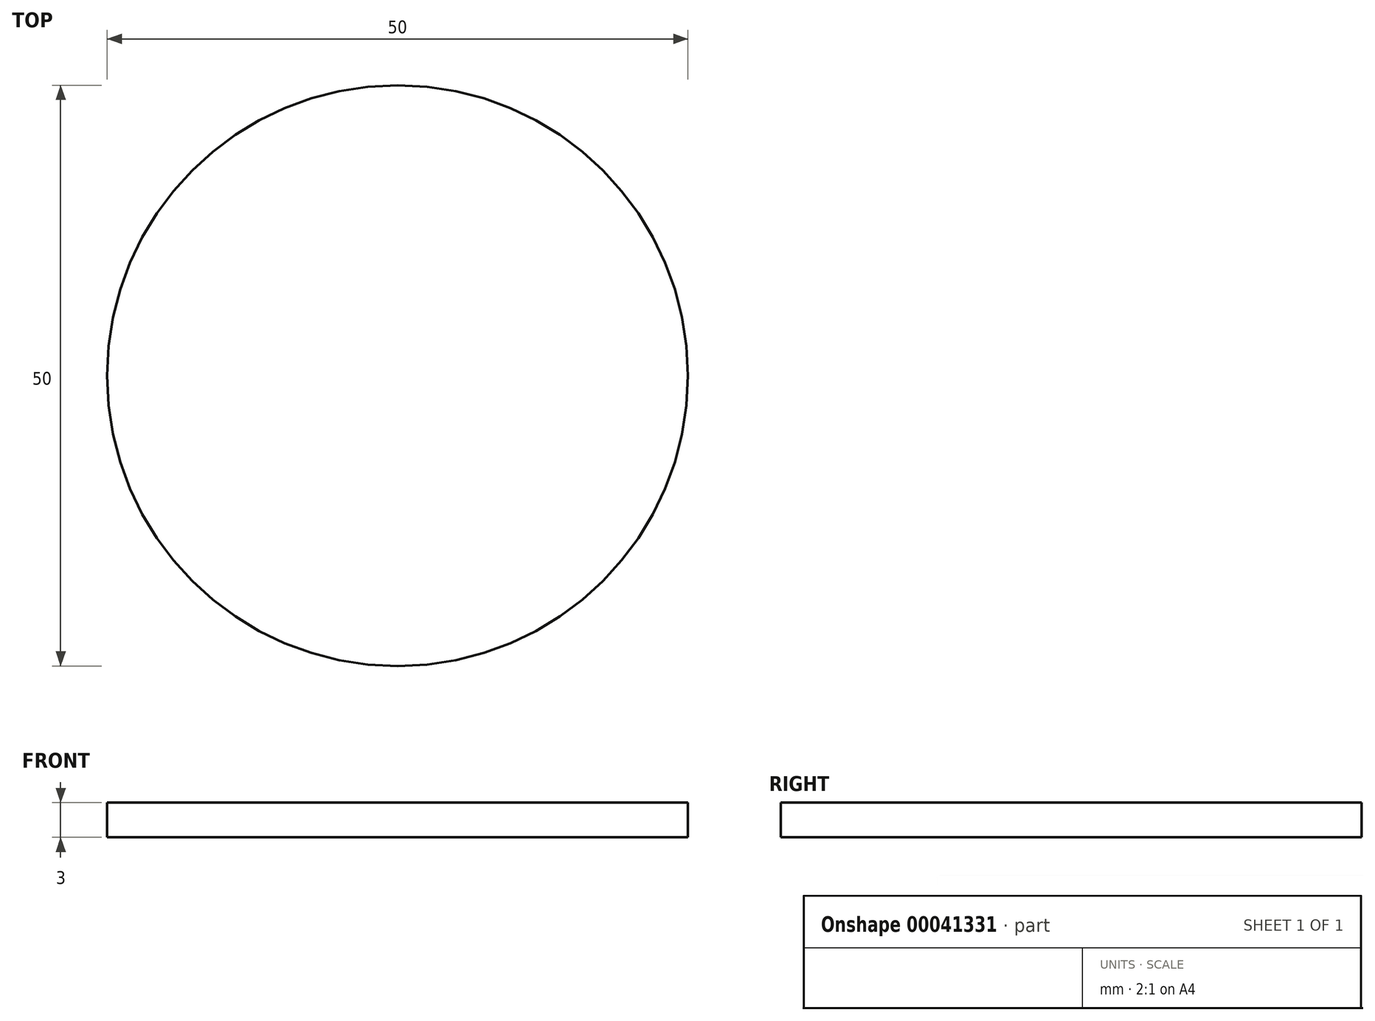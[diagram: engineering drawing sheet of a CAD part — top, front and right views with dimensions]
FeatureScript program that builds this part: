
annotation { "Feature Type Name" : "Feature", "Feature Type Description" : "" }
export const myFeature = defineFeature(function(context is Context, id is Id, definition is map)
    precondition{}
    {
        {
            var Q0;
            Q0=qCreatedBy(makeId("Front.planeOp"),FACE);
            var sketch = newSketch(context, id + "F0", { "sketchPlane" : qUnion([Q0])});
            skLineSegment(sketch, "E0", {"start": v(0, 0) * mm, "end": v(-25, 0) * mm});
            skLineSegment(sketch, "E1", {"start": v(-25, 0) * mm, "end": v(-25, 3) * mm});
            skLineSegment(sketch, "E2", {"start": v(-25, 3) * mm, "end": v(0, 3) * mm});
            skLineSegment(sketch, "E3", {"start": v(0, 3) * mm, "end": v(0, 0) * mm});
            skSolve(sketch);
        }
        {
            var Q0;
            Q0=makeQuery(id+"F0.imprint","IMPRINT",FACE,{"disambiguationData":[TD([[makeQuery(id+"F0.imprint","IMPRINT",EDGE,{"derivedFrom":sQuery(id+"F0.wireOp",EDGE,"E0")}),-1.0]])]});
            var Q1;
            Q1=sQuery(id+"F0.wireOp",EDGE,"E3");
            revolve(context, id + "F1", {"entities" : qUnion([Q0]), "axis" : qUnion([Q1]), "revolveType" : RevolveType.FULL});
        }
    });
